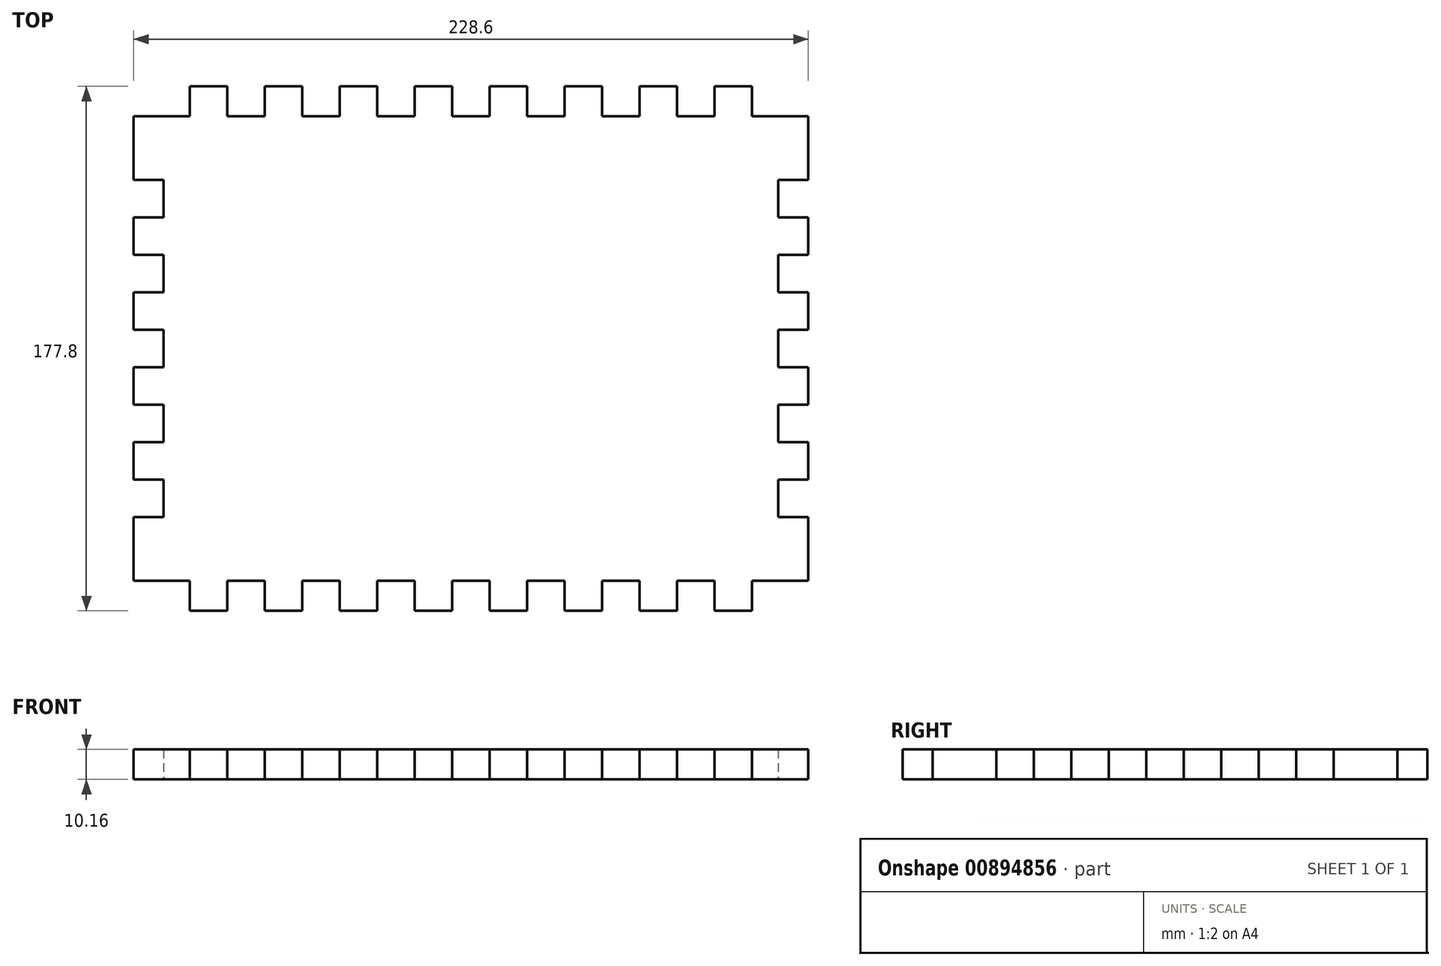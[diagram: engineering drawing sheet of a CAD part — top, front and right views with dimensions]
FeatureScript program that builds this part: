
annotation { "Feature Type Name" : "Feature", "Feature Type Description" : "" }
export const myFeature = defineFeature(function(context is Context, id is Id, definition is map)
    precondition{}
    {
        {
            var Q0;
            Q0=qCreatedBy(makeId("Top.planeOp"),FACE);
            var sketch = newSketch(context, id + "F0", { "sketchPlane" : qUnion([Q0])});
            skLineSegment(sketch, "E0.bottom", {"start": v(19.05, 0) * mm, "end": v(31.75, 0) * mm});
            skLineSegment(sketch, "E0.left", {"start": v(0, -10.16) * mm, "end": v(0, -31.75) * mm});
            skLineSegment(sketch, "E1", {"start": v(0, -10.16) * mm, "end": v(19.05, -10.16) * mm});
            skLineSegment(sketch, "E2", {"start": v(19.05, -10.16) * mm, "end": v(19.05, 0) * mm});
            skLineSegment(sketch, "E3", {"start": v(31.75, 0) * mm, "end": v(31.75, -10.16) * mm});
            skLineSegment(sketch, "E4", {"start": v(31.75, -10.16) * mm, "end": v(44.45, -10.16) * mm});
            skLineSegment(sketch, "E5", {"start": v(44.45, -10.16) * mm, "end": v(44.45, 0) * mm});
            skLineSegment(sketch, "E6", {"start": v(44.45, 0) * mm, "end": v(57.15, 0) * mm});
            skLineSegment(sketch, "E7", {"start": v(57.15, 0) * mm, "end": v(57.15, -10.16) * mm});
            skLineSegment(sketch, "E8", {"start": v(57.15, -10.16) * mm, "end": v(69.85, -10.16) * mm});
            skLineSegment(sketch, "E9", {"start": v(69.85, -10.16) * mm, "end": v(69.85, 0) * mm});
            skLineSegment(sketch, "E10", {"start": v(69.85, 0) * mm, "end": v(82.55, 0) * mm});
            skLineSegment(sketch, "E11", {"start": v(82.55, 0) * mm, "end": v(82.55, -10.16) * mm});
            skLineSegment(sketch, "E12", {"start": v(82.55, -10.16) * mm, "end": v(95.25, -10.16) * mm});
            skLineSegment(sketch, "E13", {"start": v(95.25, -10.16) * mm, "end": v(95.25, 0) * mm});
            skLineSegment(sketch, "E14", {"start": v(95.25, 0) * mm, "end": v(107.95, 0) * mm});
            skLineSegment(sketch, "E15", {"start": v(107.95, 0) * mm, "end": v(107.95, -10.16) * mm});
            skLineSegment(sketch, "E16", {"start": v(107.95, -10.16) * mm, "end": v(120.65, -10.16) * mm});
            skLineSegment(sketch, "E17", {"start": v(120.65, -10.16) * mm, "end": v(120.65, 0) * mm});
            skLineSegment(sketch, "E18.trimOffspring", {"start": v(120.65, 0) * mm, "end": v(133.35, 0) * mm});
            skPoint(sketch, "E19.orphan", {"position": v(0, 0) * mm});
            skLineSegment(sketch, "E20", {"start": v(133.35, 0) * mm, "end": v(133.35, -10.16) * mm});
            skLineSegment(sketch, "E21", {"start": v(133.35, -10.16) * mm, "end": v(146.05, -10.16) * mm});
            skLineSegment(sketch, "E22", {"start": v(146.05, -10.16) * mm, "end": v(146.05, 0) * mm});
            skLineSegment(sketch, "E23", {"start": v(146.05, 0) * mm, "end": v(158.75, 0) * mm});
            skLineSegment(sketch, "E24", {"start": v(158.75, 0) * mm, "end": v(158.75, -10.16) * mm});
            skLineSegment(sketch, "E25", {"start": v(158.75, -10.16) * mm, "end": v(171.45, -10.16) * mm});
            skLineSegment(sketch, "E26", {"start": v(171.45, -10.16) * mm, "end": v(171.45, 0) * mm});
            skLineSegment(sketch, "E27", {"start": v(171.45, 0) * mm, "end": v(184.15, 0) * mm});
            skLineSegment(sketch, "E28", {"start": v(184.15, 0) * mm, "end": v(184.15, -10.16) * mm});
            skLineSegment(sketch, "E29", {"start": v(184.15, -10.16) * mm, "end": v(196.85, -10.16) * mm});
            skLineSegment(sketch, "E30", {"start": v(196.85, -10.16) * mm, "end": v(196.85, 0) * mm});
            skLineSegment(sketch, "E31.trimOffspring", {"start": v(196.85, 0) * mm, "end": v(209.55, 0) * mm});
            skLineSegment(sketch, "E32", {"start": v(209.55, 0) * mm, "end": v(209.55, -10.16) * mm});
            skLineSegment(sketch, "E33", {"start": v(209.55, -10.16) * mm, "end": v(228.6, -10.16) * mm});
            skPoint(sketch, "E34.orphan", {"position": v(228.6, 0) * mm});
            skLineSegment(sketch, "E35", {"start": v(0, -31.75) * mm, "end": v(10.16, -31.75) * mm});
            skLineSegment(sketch, "E36", {"start": v(10.16, -31.75) * mm, "end": v(10.16, -44.45) * mm});
            skLineSegment(sketch, "E37", {"start": v(10.16, -44.45) * mm, "end": v(0, -44.45) * mm});
            skLineSegment(sketch, "E38", {"start": v(0, -44.45) * mm, "end": v(0, -57.15) * mm});
            skLineSegment(sketch, "E39", {"start": v(0, -57.15) * mm, "end": v(10.16, -57.15) * mm});
            skLineSegment(sketch, "E40", {"start": v(10.16, -57.15) * mm, "end": v(10.16, -69.85) * mm});
            skLineSegment(sketch, "E41", {"start": v(10.16, -69.85) * mm, "end": v(0, -69.85) * mm});
            skLineSegment(sketch, "E42", {"start": v(0, -69.85) * mm, "end": v(0, -82.55) * mm});
            skLineSegment(sketch, "E43", {"start": v(0, -82.55) * mm, "end": v(10.16, -82.55) * mm});
            skLineSegment(sketch, "E44", {"start": v(10.16, -82.55) * mm, "end": v(10.16, -95.25) * mm});
            skLineSegment(sketch, "E45", {"start": v(10.16, -95.25) * mm, "end": v(0, -95.25) * mm});
            skLineSegment(sketch, "E46", {"start": v(0, -95.25) * mm, "end": v(0, -107.95) * mm});
            skLineSegment(sketch, "E47", {"start": v(0, -107.95) * mm, "end": v(10.16, -107.95) * mm});
            skLineSegment(sketch, "E48", {"start": v(10.16, -107.95) * mm, "end": v(10.16, -120.65) * mm});
            skLineSegment(sketch, "E49", {"start": v(10.16, -120.65) * mm, "end": v(0, -120.65) * mm});
            skLineSegment(sketch, "E50.trimOffspring", {"start": v(0, -120.65) * mm, "end": v(0, -133.35) * mm});
            skLineSegment(sketch, "E51", {"start": v(0, -133.35) * mm, "end": v(10.16, -133.35) * mm});
            skLineSegment(sketch, "E52", {"start": v(10.16, -133.35) * mm, "end": v(10.16, -146.05) * mm});
            skLineSegment(sketch, "E53", {"start": v(10.16, -146.05) * mm, "end": v(0, -146.05) * mm});
            skLineSegment(sketch, "E54", {"start": v(0, -146.05) * mm, "end": v(0, -167.64) * mm});
            skLineSegment(sketch, "E55", {"start": v(0, -167.64) * mm, "end": v(19.05, -167.64) * mm});
            skLineSegment(sketch, "E56", {"start": v(19.05, -167.64) * mm, "end": v(19.05, -167.64) * mm});
            skPoint(sketch, "E57.orphan", {"position": v(0, -177.8) * mm});
            skLineSegment(sketch, "E58", {"start": v(114.3, -10.16) * mm, "end": v(114.3, -46) * mm, "construction": true});
            skLineSegment(sketch, "E59", {"start": v(10.16, -88.9) * mm, "end": v(46.1, -88.9) * mm, "construction": true});
            skLineSegment(sketch, "E60.MirrorCS", {"start": v(228.6, -10.16) * mm, "end": v(209.55, -10.16) * mm});
            skLineSegment(sketch, "E61.MirrorCS", {"start": v(218.44, -69.85) * mm, "end": v(228.6, -69.85) * mm});
            skLineSegment(sketch, "E62.MirrorCS", {"start": v(218.44, -107.95) * mm, "end": v(218.44, -120.65) * mm});
            skLineSegment(sketch, "E63.MirrorCS", {"start": v(228.6, -57.15) * mm, "end": v(218.44, -57.15) * mm});
            skLineSegment(sketch, "E64.MirrorCS", {"start": v(218.44, -44.45) * mm, "end": v(228.6, -44.45) * mm});
            skLineSegment(sketch, "E65.MirrorCS", {"start": v(218.44, -95.25) * mm, "end": v(228.6, -95.25) * mm});
            skLineSegment(sketch, "E66.MirrorCS", {"start": v(228.6, -31.75) * mm, "end": v(218.44, -31.75) * mm});
            skLineSegment(sketch, "E67.MirrorCS", {"start": v(228.6, -82.55) * mm, "end": v(218.44, -82.55) * mm});
            skLineSegment(sketch, "E68.MirrorCS", {"start": v(218.44, -120.65) * mm, "end": v(228.6, -120.65) * mm});
            skLineSegment(sketch, "E69.MirrorCS", {"start": v(228.6, -107.95) * mm, "end": v(218.44, -107.95) * mm});
            skLineSegment(sketch, "E70.MirrorCS", {"start": v(228.6, -133.35) * mm, "end": v(218.44, -133.35) * mm});
            skLineSegment(sketch, "E71.MirrorCS", {"start": v(218.44, -146.05) * mm, "end": v(228.6, -146.05) * mm});
            skLineSegment(sketch, "E72.MirrorCS", {"start": v(218.44, -82.55) * mm, "end": v(218.44, -95.25) * mm});
            skLineSegment(sketch, "E73.MirrorCS", {"start": v(228.6, -120.65) * mm, "end": v(228.6, -133.35) * mm});
            skLineSegment(sketch, "E74.MirrorCS", {"start": v(228.6, -146.05) * mm, "end": v(228.6, -167.64) * mm});
            skLineSegment(sketch, "E75.MirrorCS", {"start": v(228.6, -44.45) * mm, "end": v(228.6, -57.15) * mm});
            skLineSegment(sketch, "E76.MirrorCS", {"start": v(228.6, -10.16) * mm, "end": v(228.6, -31.75) * mm});
            skLineSegment(sketch, "E77.MirrorCS", {"start": v(228.6, -69.85) * mm, "end": v(228.6, -82.55) * mm});
            skLineSegment(sketch, "E78.MirrorCS", {"start": v(228.6, -95.25) * mm, "end": v(228.6, -107.95) * mm});
            skLineSegment(sketch, "E79.MirrorCS", {"start": v(209.55, -167.64) * mm, "end": v(209.55, -167.64) * mm});
            skLineSegment(sketch, "E80.MirrorCS", {"start": v(228.6, -167.64) * mm, "end": v(209.55, -167.64) * mm});
            skLineSegment(sketch, "E81.MirrorCS", {"start": v(218.44, -57.15) * mm, "end": v(218.44, -69.85) * mm});
            skLineSegment(sketch, "E82.MirrorCS", {"start": v(218.44, -133.35) * mm, "end": v(218.44, -146.05) * mm});
            skLineSegment(sketch, "E83.MirrorCS", {"start": v(218.44, -31.75) * mm, "end": v(218.44, -44.45) * mm});
            skLineSegment(sketch, "E84.MirrorCS", {"start": v(209.55, -177.8) * mm, "end": v(209.55, -167.64) * mm});
            skLineSegment(sketch, "E85.MirrorCS", {"start": v(69.85, -167.64) * mm, "end": v(69.85, -177.8) * mm});
            skLineSegment(sketch, "E86.MirrorCS", {"start": v(107.95, -177.8) * mm, "end": v(107.95, -167.64) * mm});
            skLineSegment(sketch, "E87.MirrorCS", {"start": v(184.15, -177.8) * mm, "end": v(184.15, -167.64) * mm});
            skLineSegment(sketch, "E88.MirrorCS", {"start": v(57.15, -177.8) * mm, "end": v(57.15, -167.64) * mm});
            skLineSegment(sketch, "E89.MirrorCS", {"start": v(120.65, -167.64) * mm, "end": v(120.65, -177.8) * mm});
            skLineSegment(sketch, "E90.MirrorCS", {"start": v(196.85, -167.64) * mm, "end": v(196.85, -177.8) * mm});
            skLineSegment(sketch, "E91.MirrorCS", {"start": v(171.45, -167.64) * mm, "end": v(171.45, -177.8) * mm});
            skLineSegment(sketch, "E92.MirrorCS", {"start": v(44.45, -167.64) * mm, "end": v(44.45, -177.8) * mm});
            skLineSegment(sketch, "E93.MirrorCS", {"start": v(19.05, -167.64) * mm, "end": v(19.05, -177.8) * mm});
            skLineSegment(sketch, "E94.MirrorCS", {"start": v(146.05, -167.64) * mm, "end": v(146.05, -177.8) * mm});
            skLineSegment(sketch, "E95.MirrorCS", {"start": v(95.25, -167.64) * mm, "end": v(95.25, -177.8) * mm});
            skLineSegment(sketch, "E96.MirrorCS", {"start": v(31.75, -177.8) * mm, "end": v(31.75, -167.64) * mm});
            skLineSegment(sketch, "E97.MirrorCS", {"start": v(133.35, -177.8) * mm, "end": v(133.35, -167.64) * mm});
            skLineSegment(sketch, "E98.MirrorCS", {"start": v(82.55, -177.8) * mm, "end": v(82.55, -167.64) * mm});
            skLineSegment(sketch, "E99.MirrorCS", {"start": v(158.75, -177.8) * mm, "end": v(158.75, -167.64) * mm});
            skLineSegment(sketch, "E100.MirrorCS", {"start": v(69.85, -177.8) * mm, "end": v(82.55, -177.8) * mm});
            skLineSegment(sketch, "E101.MirrorCS", {"start": v(95.25, -177.8) * mm, "end": v(107.95, -177.8) * mm});
            skLineSegment(sketch, "E102.MirrorCS", {"start": v(196.85, -177.8) * mm, "end": v(209.55, -177.8) * mm});
            skLineSegment(sketch, "E103.MirrorCS", {"start": v(44.45, -177.8) * mm, "end": v(57.15, -177.8) * mm});
            skLineSegment(sketch, "E104.MirrorCS", {"start": v(146.05, -177.8) * mm, "end": v(158.75, -177.8) * mm});
            skLineSegment(sketch, "E105.MirrorCS", {"start": v(19.05, -177.8) * mm, "end": v(31.75, -177.8) * mm});
            skLineSegment(sketch, "E106.MirrorCS", {"start": v(171.45, -177.8) * mm, "end": v(184.15, -177.8) * mm});
            skLineSegment(sketch, "E107.MirrorCS", {"start": v(120.65, -177.8) * mm, "end": v(133.35, -177.8) * mm});
            skLineSegment(sketch, "E108.MirrorCS", {"start": v(107.95, -167.64) * mm, "end": v(120.65, -167.64) * mm});
            skLineSegment(sketch, "E109.MirrorCS", {"start": v(57.15, -167.64) * mm, "end": v(69.85, -167.64) * mm});
            skLineSegment(sketch, "E110.MirrorCS", {"start": v(133.35, -167.64) * mm, "end": v(146.05, -167.64) * mm});
            skLineSegment(sketch, "E111.MirrorCS", {"start": v(82.55, -167.64) * mm, "end": v(95.25, -167.64) * mm});
            skLineSegment(sketch, "E112.MirrorCS", {"start": v(158.75, -167.64) * mm, "end": v(171.45, -167.64) * mm});
            skLineSegment(sketch, "E113.MirrorCS", {"start": v(184.15, -167.64) * mm, "end": v(196.85, -167.64) * mm});
            skLineSegment(sketch, "E114.MirrorCS", {"start": v(31.75, -167.64) * mm, "end": v(44.45, -167.64) * mm});
            skSolve(sketch);
        }
        {
            var Q0;
            Q0=makeQuery(id+"F0.imprint","IMPRINT",FACE,{"disambiguationData":[TD([[makeQuery(id+"F0.imprint","IMPRINT",EDGE,{"derivedFrom":sQuery(id+"F0.wireOp",EDGE,"E1")}),-1.0]])]});
            extrude(context, id + "F1", {"entities" : qUnion([Q0]), "depth" : 10.16 * mm, "offsetDistance" : 25.4 * mm});
        }
    });
